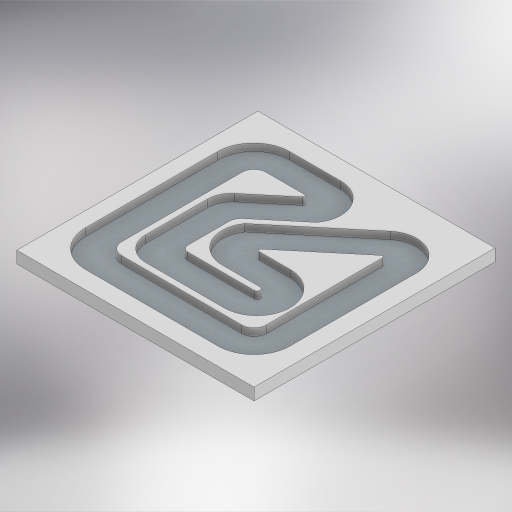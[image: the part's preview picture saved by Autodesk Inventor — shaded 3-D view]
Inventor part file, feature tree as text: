
AUTODESK INVENTOR PART (.ipt)
format: ipt  version: 2024.2 (Build 282272000, 272)  size: 393,728 bytes
history: native  units: mm
features: other x2, sketch x2, extrude x2
ambient origin geometry x8: Origin, YZ Plane, XZ Plane, XY Plane, X Axis, Y Axis, Z Axis, Center Point
bodies: Body1 (feature_tree)
feature tree (6):
  other  "Sólido1"
  sketch  "Boceto2"  dims[d2=10000.0mm d21=3000.0mm d22=500.0mm d23=150.0mm d24=2000.0mm d25=2000.0mm d26=1000.0mm d27=1000.0mm d28=0.0mm d29=600.0mm d30=0.0mm]
  extrude  "Extrusión1"  Depth=10000.0mm
  extrude  "Extrusión2"  Depth=3000.0mm
  sketch  "Boceto1"  dims[d0=10000.0mm d1=10000.0mm]
  other  "Finish1"
